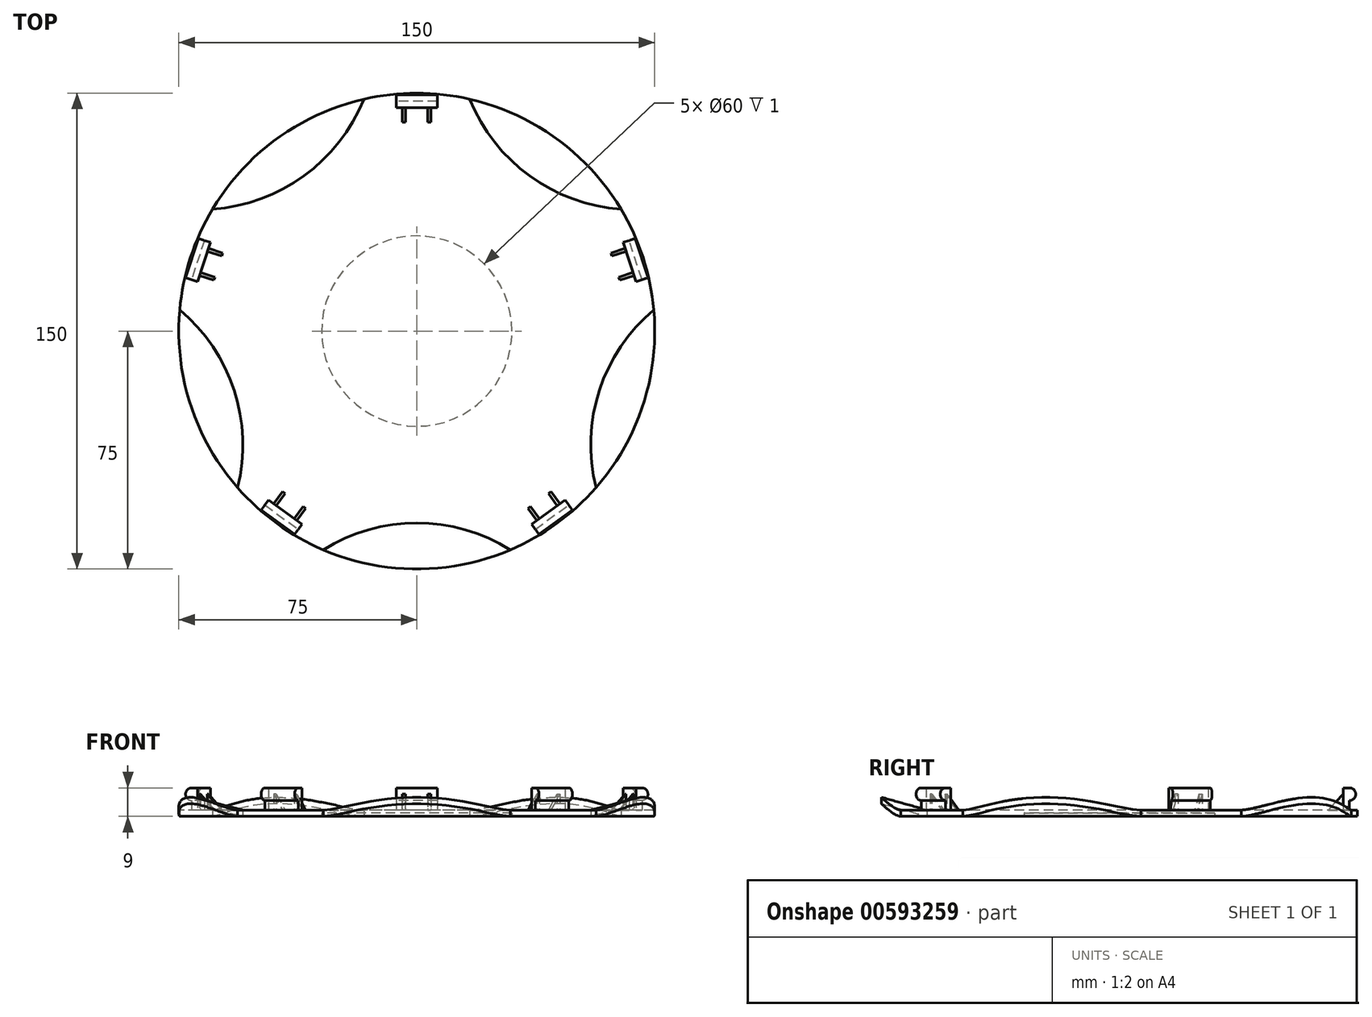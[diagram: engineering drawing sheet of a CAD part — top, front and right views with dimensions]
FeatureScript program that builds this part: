
annotation { "Feature Type Name" : "Feature", "Feature Type Description" : "" }
export const myFeature = defineFeature(function(context is Context, id is Id, definition is map)
    precondition{}
    {
        {
            var Q0;
            Q0=qCreatedBy(makeId("Top.planeOp"),FACE);
            var sketch = newSketch(context, id + "F0", { "sketchPlane" : qUnion([Q0])});
            skCircle(sketch, "E0", {"center": v(0, 0) * mm, "radius": 75.5 * mm});
            skLineSegment(sketch, "E1.bottom", {"start": v(-6.5, 72.5) * mm, "end": v(6.5, 72.5) * mm});
            skLineSegment(sketch, "E1.top", {"start": v(-6.5, 70.5) * mm, "end": v(6.5, 70.5) * mm});
            skLineSegment(sketch, "E1.left", {"start": v(-6.5, 72.5) * mm, "end": v(-6.5, 70.5) * mm});
            skLineSegment(sketch, "E1.right", {"start": v(6.5, 72.5) * mm, "end": v(6.5, 70.5) * mm});
            skSolve(sketch);
        }
        {
            var Q0;
            Q0=makeQuery(id+"F0.imprint","IMPRINT",FACE,{"disambiguationData":[TD([[makeQuery(id+"F0.imprint","IMPRINT",EDGE,{"derivedFrom":sQuery(id+"F0.wireOp",EDGE,"E0")}),1.0]])]});
            var Q1;
            Q1=makeQuery(id+"F0.imprint","IMPRINT",FACE,{"disambiguationData":[TD([[makeQuery(id+"F0.imprint","IMPRINT",EDGE,{"derivedFrom":sQuery(id+"F0.wireOp",EDGE,"E1.bottom")}),-1.0]])]});
            extrude(context, id + "F1", {"entities" : qUnion([Q0, Q1]), "depth" : 2 * mm, "offsetDistance" : 25 * mm});
        }
        {
            var Q0;
            Q0=makeQuery(id+"F0.imprint","IMPRINT",FACE,{"disambiguationData":[TD([[makeQuery(id+"F0.imprint","IMPRINT",EDGE,{"derivedFrom":sQuery(id+"F0.wireOp",EDGE,"E1.bottom")}),-1.0]])]});
            extrude(context, id + "F2", {"entities" : qUnion([Q0]), "operationType" : NewBodyOperationType.ADD, "depth" : 9 * mm, "offsetDistance" : 25 * mm});
        }
        {
            var Q0;
            Q0=makeQuery(id+"F2.opExtrude","SWEPT_FACE",FACE,{"disambiguationData":[OSD([sQuery(id+"F0.wireOp",EDGE,"E1.left")])]});
            var sketch = newSketch(context, id + "F3", { "sketchPlane" : qUnion([Q0])});
            skCircle(sketch, "E2", {"center": v(-72.5, 7) * mm, "radius": 2 * mm});
            skSolve(sketch);
        }
        {
            var Q0;
            {var subQ0=sQuery(id+"F3.wireOp",EDGE,"E2");var subQ1=sQuery(id+"F0.wireOp",EDGE,"E1.left");var subQ2=makeQuery(id+"F2.opExtrude","SWEPT_EDGE",EDGE,{"disambiguationData":[OSD([sQuery(id+"F0.wireOp",EDGE,"E1.bottom"),subQ1])]});var subQ4=makeQuery(id+"F3.imprint","INTERSECT",VERTEX,{"derivedFrom":[subQ2,subQ0]});Q0=makeQuery(id+"F3.imprint","IMPRINT",FACE,{"disambiguationData":[TD([[makeQuery(id+"F3.imprint","IMPRINT",EDGE,{"disambiguationData":[TD([[subQ4,1.0]])],"derivedFrom":subQ0}),1.0]])]});}
            extrude(context, id + "F4", {"entities" : qUnion([Q0]), "operationType" : NewBodyOperationType.ADD, "oppositeDirection" : true, "depth" : 13 * mm, "offsetDistance" : 25 * mm});
        }
        {
            var Q0;
            Q0=makeQuery(id+"F4.boolean.opBoolean","MERGE",FACE,{"derivedFrom":[makeQuery(id+"F2.opExtrude","SWEPT_FACE",FACE,{"disambiguationData":[OSD([sQuery(id+"F0.wireOp",EDGE,"E1.right")])]}),makeQuery(id+"F4.opExtrude","CAP_FACE",FACE,{"disambiguationData":[OSD([sQuery(id+"F0.wireOp",EDGE,"E1.bottom"),sQuery(id+"F0.wireOp",EDGE,"E1.left"),sQuery(id+"F3.wireOp",EDGE,"E2")])],"isStart":false})]});
            cPlane(context, id + "F5", {"entities" : qUnion([Q0]), "cplaneType" : CPlaneType.OFFSET, "offset" : 2 * mm, "oppositeDirection" : true, "width" : 150 * mm, "height" : 150 * mm});
        }
        {
            var Q0;
            Q0=qCreatedBy(id+"F5.planeOp",FACE);
            var sketch = newSketch(context, id + "F6", { "sketchPlane" : qUnion([Q0])});
            skLineSegment(sketch, "E3.0", {"start": v(-75.5, 2) * mm, "end": v(75.5, 2) * mm});
            skLineSegment(sketch, "E4.0", {"start": v(70.5, 9) * mm, "end": v(70.5, 2) * mm});
            skLineSegment(sketch, "E5", {"start": v(70.5, 7) * mm, "end": v(65.8, 2) * mm});
            skLineSegment(sketch, "E6", {"start": v(65.8, 2) * mm, "end": v(70.5, 2) * mm});
            skSolve(sketch);
        }
        {
            var Q0;
            {var subQ2=sQuery(id+"F6.wireOp",EDGE,"E5");Q0=makeQuery(id+"F6.imprint","IMPRINT",FACE,{"disambiguationData":[TD([[makeQuery(id+"F6.imprint","IMPRINT",EDGE,{"derivedFrom":subQ2}),1.0]])]});}
            extrude(context, id + "F7", {"entities" : qUnion([Q0]), "operationType" : NewBodyOperationType.ADD, "oppositeDirection" : true, "depth" : 1 * mm, "offsetDistance" : 25 * mm});
        }
        {
            var Q0;
            {var subQ0=sQuery(id+"F0.wireOp",EDGE,"E1.left");Q0=makeQuery(id+"F4.boolean.opBoolean","MERGE",FACE,{"derivedFrom":[makeQuery(id+"F2.opExtrude","SWEPT_FACE",FACE,{"disambiguationData":[OSD([subQ0])]}),makeQuery(id+"F4.opExtrude","CAP_FACE",FACE,{"disambiguationData":[OSD([sQuery(id+"F0.wireOp",EDGE,"E1.bottom"),subQ0,sQuery(id+"F3.wireOp",EDGE,"E2")])],"isStart":true})]});}
            cPlane(context, id + "F8", {"entities" : qUnion([Q0]), "cplaneType" : CPlaneType.OFFSET, "offset" : 2 * mm, "oppositeDirection" : true, "width" : 150 * mm, "height" : 150 * mm});
        }
        {
            var Q0;
            Q0=qCreatedBy(id+"F8.planeOp",FACE);
            var sketch = newSketch(context, id + "F9", { "sketchPlane" : qUnion([Q0])});
            skPoint(sketch, "E7.0", {"position": v(-70.5, 7) * mm});
            skPoint(sketch, "E8.0", {"position": v(-70.5, 2) * mm});
            skPoint(sketch, "E9.0", {"position": v(-65.8, 2) * mm});
            skLineSegment(sketch, "E10", {"start": v(-70.5, 7) * mm, "end": v(-70.5, 2) * mm});
            skLineSegment(sketch, "E11", {"start": v(-65.8, 2) * mm, "end": v(-70.5, 7) * mm});
            skLineSegment(sketch, "E12", {"start": v(-65.8, 2) * mm, "end": v(-70.5, 2) * mm});
            skSolve(sketch);
        }
        {
            var Q0;
            Q0=makeQuery(id+"F9.imprint","IMPRINT",FACE,{"disambiguationData":[TD([[makeQuery(id+"F9.imprint","IMPRINT",EDGE,{"derivedFrom":sQuery(id+"F9.wireOp",EDGE,"E10")}),1.0]])]});
            extrude(context, id + "F10", {"entities" : qUnion([Q0]), "operationType" : NewBodyOperationType.ADD, "oppositeDirection" : true, "depth" : 1 * mm, "offsetDistance" : 25 * mm});
        }
        {
            var Q0;
            Q0=qCreatedBy(makeId("Right.planeOp"),FACE);
            var sketch = newSketch(context, id + "F11", { "sketchPlane" : qUnion([Q0])});
            skLineSegment(sketch, "E13", {"start": v(0, 44.58) * mm, "end": v(0, -35.66) * mm, "construction": true});
            skSolve(sketch);
        }
        {
            var Q0;
            Q0=makeQuery(id+"F1.opExtrude","SWEPT_BODY",BODY,{"disambiguationData":[OSD([sQuery(id+"F0.wireOp",EDGE,"E0")])]});
            var Q1;
            Q1=sQuery(id+"F11.wireOp",EDGE,"E13");
            circularPattern(context, id + "F12", {"entities" : qUnion([Q0]), "axis" : qUnion([Q1]), "angle" : 360 * degree, "instanceCount" : 5, "equalSpace" : true});
        }
        {
            var Q0;
            Q0=makeQuery(id+"F0.imprint","IMPRINT",FACE,{"disambiguationData":[TD([[makeQuery(id+"F0.imprint","IMPRINT",EDGE,{"derivedFrom":sQuery(id+"F0.wireOp",EDGE,"E0")}),1.0]])]});
            var sketch = newSketch(context, id + "F13", { "sketchPlane" : qUnion([Q0])});
            skCircle(sketch, "E14", {"center": v(0, 0) * mm, "radius": 30 * mm});
            skSolve(sketch);
        }
        {
            var Q0;
            Q0=makeQuery(id+"F13.imprint","IMPRINT",FACE,{"disambiguationData":[TD([[makeQuery(id+"F13.imprint","IMPRINT",EDGE,{"derivedFrom":sQuery(id+"F13.wireOp",EDGE,"E14")}),1.0]])]});
            extrude(context, id + "F14", {"entities" : qUnion([Q0]), "operationType" : NewBodyOperationType.REMOVE, "depth" : 1 * mm, "offsetDistance" : 25 * mm});
        }
        {
            var Q0;
            Q0=makeQuery(id+"F1.opExtrude","CAP_FACE",FACE,{"disambiguationData":[OSD([sQuery(id+"F0.wireOp",EDGE,"E0")])],"isStart":false});
            var sketch = newSketch(context, id + "F15", { "sketchPlane" : qUnion([Q0])});
            skArc(sketch, "E15", {"start": v(30, -69.28) * mm, "mid": v(0, -60.5) * mm, "end": v(-30, -69.28) * mm});
            skSolve(sketch);
        }
        {
            var Q0;
            Q0=makeQuery(id+"F0.imprint","IMPRINT",FACE,{"disambiguationData":[TD([[makeQuery(id+"F0.imprint","IMPRINT",EDGE,{"derivedFrom":sQuery(id+"F0.wireOp",EDGE,"E0")}),1.0]])]});
            var sketch = newSketch(context, id + "F16", { "sketchPlane" : qUnion([Q0])});
            skArc(sketch, "E16.0", {"start": v(30, -69.28) * mm, "mid": v(0, -60.5) * mm, "end": v(-30, -69.28) * mm});
            skPoint(sketch, "E17", {"position": v(0, -74.93) * mm});
            skArc(sketch, "E18.1.0", {"start": v(75.16, 7.12) * mm, "mid": v(57.54, -18.7) * mm, "end": v(56.62, -49.94) * mm});
            skArc(sketch, "E18.2.0", {"start": v(16.45, 73.69) * mm, "mid": v(35.56, 48.95) * mm, "end": v(65, 38.42) * mm});
            skArc(sketch, "E18.3.0", {"start": v(-65, 38.42) * mm, "mid": v(-35.56, 48.95) * mm, "end": v(-16.45, 73.69) * mm});
            skArc(sketch, "E18.4.0", {"start": v(-56.62, -49.94) * mm, "mid": v(-57.54, -18.7) * mm, "end": v(-75.16, 7.12) * mm});
            skPoint(sketch, "E18.center", {"position": v(0, 0) * mm});
            skSolve(sketch);
        }
        {
            var Q0;
            Q0=qCreatedBy(makeId("Front.planeOp"),FACE);
            cPlane(context, id + "F17", {"entities" : qUnion([Q0]), "cplaneType" : CPlaneType.OFFSET, "offset" : 75 * mm, "width" : 150 * mm, "height" : 150 * mm});
        }
        {
            var Q0;
            Q0=qCreatedBy(id+"F17.planeOp",FACE);
            var sketch = newSketch(context, id + "F18", { "sketchPlane" : qUnion([Q0])});
            skPoint(sketch, "E19.0", {"position": v(-30, 2) * mm});
            skPoint(sketch, "E20.0", {"position": v(-30, 0) * mm});
            skPoint(sketch, "E21.0", {"position": v(30, 2) * mm});
            skPoint(sketch, "E22.0", {"position": v(30, 0) * mm});
            skLineSegment(sketch, "E23.0", {"start": v(30, 0) * mm, "end": v(-30, 0) * mm});
            skArc(sketch, "E24", {"start": v(30, 2) * mm, "mid": v(0, 6) * mm, "end": v(-30, 2) * mm});
            skArc(sketch, "E25", {"start": v(30, 0) * mm, "mid": v(0, 4) * mm, "end": v(-30, 0) * mm});
            skLineSegment(sketch, "E26", {"start": v(-30, 2) * mm, "end": v(-30, 0) * mm});
            skLineSegment(sketch, "E27", {"start": v(30, 2) * mm, "end": v(30, 0) * mm});
            skSolve(sketch);
        }
        {
            var Q0;
            {var subQ0=sQuery(id+"F15.wireOp",EDGE,"E15");Q0=makeQuery(id+"F15.imprint","IMPRINT",FACE,{"disambiguationData":[TD([[makeQuery(id+"F15.imprint","IMPRINT",EDGE,{"derivedFrom":subQ0}),1.0]])]});}
            extrude(context, id + "F19", {"entities" : qUnion([Q0]), "operationType" : NewBodyOperationType.REMOVE, "endBound" : BoundingType.THROUGH_ALL, "oppositeDirection" : true, "depth" : 25 * mm, "offsetDistance" : 25 * mm});
        }
        {
            var Q0;
            {var subQ0=sQuery(id+"F16.wireOp",EDGE,"E18.1.0");Q0=makeQuery(id+"F16.imprint","IMPRINT",FACE,{"disambiguationData":[TD([[makeQuery(id+"F16.imprint","IMPRINT",EDGE,{"derivedFrom":subQ0}),1.0]])]});}
            var Q1;
            {var subQ0=sQuery(id+"F16.wireOp",EDGE,"E18.2.0");Q1=makeQuery(id+"F16.imprint","IMPRINT",FACE,{"disambiguationData":[TD([[makeQuery(id+"F16.imprint","IMPRINT",EDGE,{"derivedFrom":subQ0}),1.0]])]});}
            var Q2;
            {var subQ0=sQuery(id+"F16.wireOp",EDGE,"E18.4.0");Q2=makeQuery(id+"F16.imprint","IMPRINT",FACE,{"disambiguationData":[TD([[makeQuery(id+"F16.imprint","IMPRINT",EDGE,{"derivedFrom":subQ0}),1.0]])]});}
            var Q3;
            {var subQ0=sQuery(id+"F16.wireOp",EDGE,"E18.3.0");Q3=makeQuery(id+"F16.imprint","IMPRINT",FACE,{"disambiguationData":[TD([[makeQuery(id+"F16.imprint","IMPRINT",EDGE,{"derivedFrom":subQ0}),1.0]])]});}
            extrude(context, id + "F20", {"entities" : qUnion([Q0, Q1, Q2, Q3]), "operationType" : NewBodyOperationType.REMOVE, "endBound" : BoundingType.THROUGH_ALL, "depth" : 25 * mm, "offsetDistance" : 25 * mm});
        }
        {
            var Q0;
            {var subQ0=sQuery(id+"F0.wireOp",EDGE,"E0");Q0=makeQuery(id+"F19.boolean.opBoolean","COPY",FACE,{"disambiguationData":[TD([makeQuery(id+"F12.opPattern","COPY",FACE,{"derivedFrom":makeQuery(id+"F1.opExtrude","SWEPT_FACE",FACE,{"disambiguationData":[OSD([subQ0])]}),"instanceName":"4"})])],"derivedFrom":makeQuery(id+"F19.opExtrude","SWEPT_FACE",FACE,{"disambiguationData":[OSD([sQuery(id+"F15.wireOp",EDGE,"E15")])]})});}
            var Q1;
            Q1=makeQuery(id+"F18.imprint","IMPRINT",FACE,{"disambiguationData":[TD([[makeQuery(id+"F18.imprint","IMPRINT",EDGE,{"derivedFrom":sQuery(id+"F18.wireOp",EDGE,"E24")}),1.0]])]});
            loft(context, id + "F21", {"sheetProfilesArray" : [{ "sheetProfileEntities" : qUnion([Q0]) }, { "sheetProfileEntities" : qUnion([Q1]) }]});
        }
        {
            var Q0;
            Q0=qCreatedBy(makeId("Front.planeOp"),FACE);
            var sketch = newSketch(context, id + "F22", { "sketchPlane" : qUnion([Q0])});
            skLineSegment(sketch, "E28", {"start": v(0, -45.04) * mm, "end": v(0, 33.9) * mm, "construction": true});
            skSolve(sketch);
        }
        {
            var Q0;
            Q0=makeQuery(id+"F21.opLoft","SWEPT_BODY",BODY,{"disambiguationData":[OSD([sQuery(id+"F15.wireOp",EDGE,"E15"),makeQuery(id+"F18.imprint","IMPRINT",FACE,{"disambiguationData":[TD([[makeQuery(id+"F18.imprint","IMPRINT",EDGE,{"derivedFrom":sQuery(id+"F18.wireOp",EDGE,"E24")}),1.0]])]})])]});
            var Q1;
            Q1=sQuery(id+"F22.wireOp",EDGE,"E28");
            circularPattern(context, id + "F23", {"entities" : qUnion([Q0]), "axis" : qUnion([Q1]), "angle" : 360 * degree, "instanceCount" : 5, "equalSpace" : true});
        }
        {
            var Q0;
            Q0=qCreatedBy(makeId("Top.planeOp"),FACE);
            var sketch = newSketch(context, id + "F24", { "sketchPlane" : qUnion([Q0])});
            skCircle(sketch, "E29", {"center": v(0, 0) * mm, "radius": 75 * mm});
            skCircle(sketch, "E30.0", {"center": v(0, 0) * mm, "radius": 98 * mm});
            skSolve(sketch);
        }
        {
            var Q0;
            Q0=makeQuery(id+"F24.imprint","IMPRINT",FACE,{"disambiguationData":[TD([[makeQuery(id+"F24.imprint","IMPRINT",EDGE,{"derivedFrom":sQuery(id+"F24.wireOp",EDGE,"E29")}),-1.0]])]});
            extrude(context, id + "F25", {"entities" : qUnion([Q0]), "operationType" : NewBodyOperationType.REMOVE, "endBound" : BoundingType.THROUGH_ALL, "depth" : 25 * mm, "offsetDistance" : 25 * mm});
        }
    });
